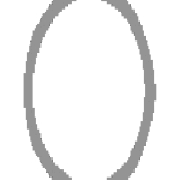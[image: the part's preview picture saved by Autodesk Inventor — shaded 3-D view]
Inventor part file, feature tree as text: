
AUTODESK INVENTOR PART (.ipt)
format: ipt  version: 2021 (Build 250183000, 183)  size: 108,544 bytes
history: native  units: in
note: dims shown in document units (in); Inventor stores cm internally (conversion verified against a paired STEP export)
features: other x4, sketch x3, plane x1
ambient origin geometry x8: Origin, YZ Plane, XZ Plane, XY Plane, X Axis, Y Axis, Z Axis, Center Point
bodies: Solid1 (feature_tree), Body (feature_tree)
feature tree (8):
  other  "Driven Length"
  other  "Frame Generator"
  other  "Start Plane"
  other  "End Plane"
  sketch  "Sketch"  dims[d2=39.5601in d4=-0.0in d5=39.5601in d6=0.12in d7=0.0in d8=90.0deg d9=39.5601in]
  sketch  "Sketch2"  dims[d0=1.0in]
  plane  "Work Plane3"
  sketch  "Sketch3"  dims[d1=0.065in]
